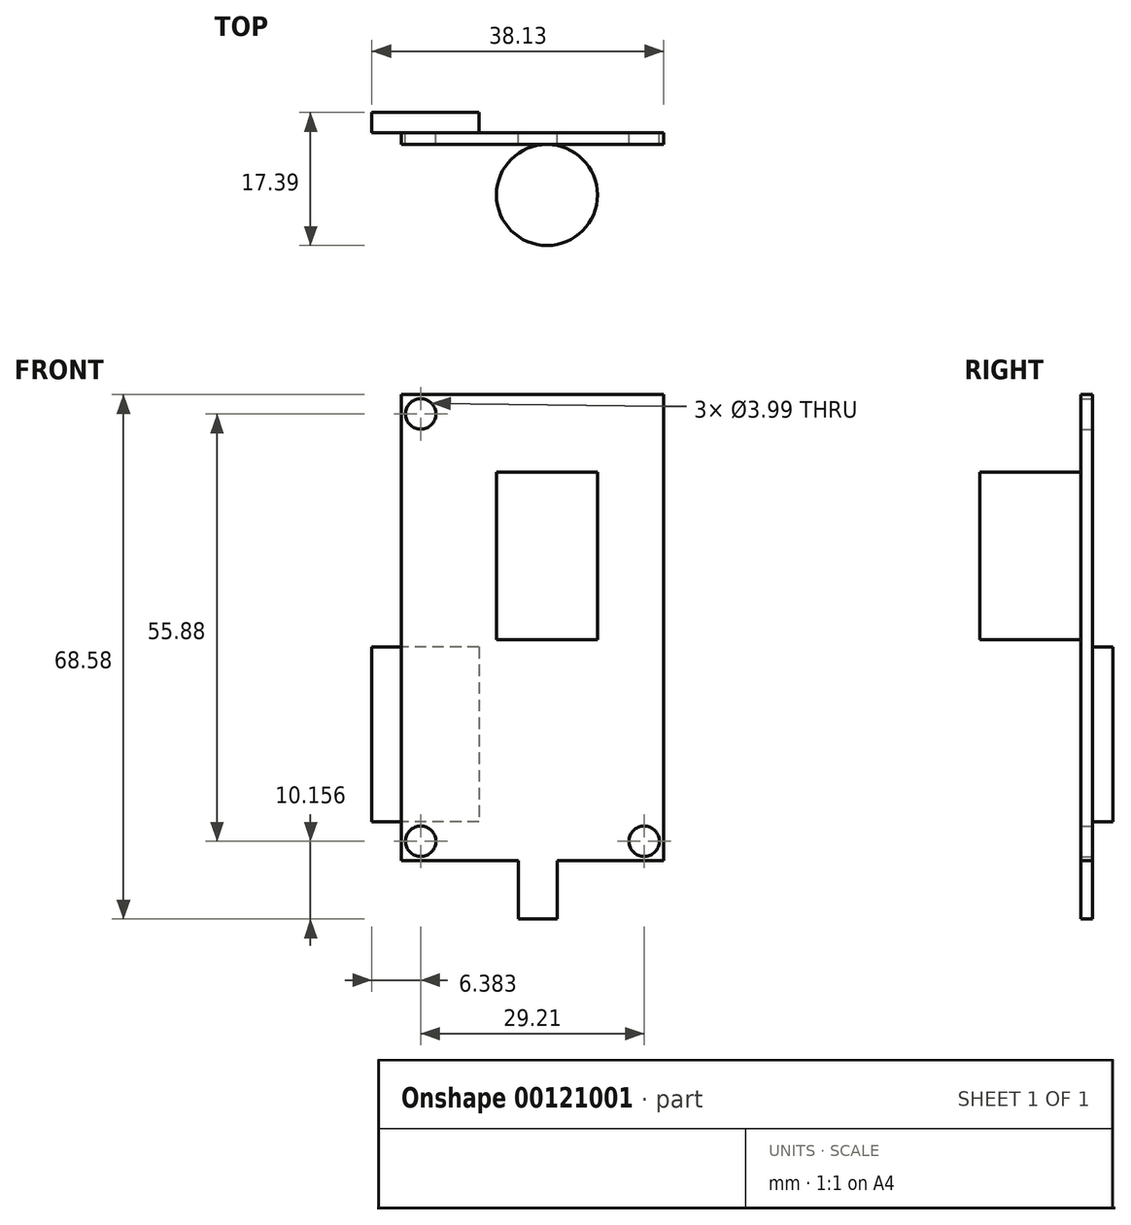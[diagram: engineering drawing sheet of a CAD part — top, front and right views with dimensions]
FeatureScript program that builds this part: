
annotation { "Feature Type Name" : "Feature", "Feature Type Description" : "" }
export const myFeature = defineFeature(function(context is Context, id is Id, definition is map)
    precondition{}
    {
        {
            var Q0;
            Q0=qCreatedBy(makeId("Front.planeOp"),FACE);
            var sketch = newSketch(context, id + "F0", { "sketchPlane" : qUnion([Q0])});
            skLineSegment(sketch, "E0.bottom", {"start": v(-17.68, 35.44) * mm, "end": v(16.61, 35.44) * mm});
            skLineSegment(sketch, "E0.top", {"start": v(-17.68, -25.52) * mm, "end": v(16.61, -25.52) * mm});
            skLineSegment(sketch, "E0.left", {"start": v(-17.68, 35.44) * mm, "end": v(-17.68, -25.52) * mm});
            skLineSegment(sketch, "E0.right", {"start": v(16.61, 35.44) * mm, "end": v(16.61, -25.52) * mm});
            skLineSegment(sketch, "E1.bottom", {"start": v(-2.36, -25.52) * mm, "end": v(2.72, -25.52) * mm});
            skLineSegment(sketch, "E1.top", {"start": v(-2.36, -33.14) * mm, "end": v(2.72, -33.14) * mm});
            skLineSegment(sketch, "E1.left", {"start": v(-2.36, -25.52) * mm, "end": v(-2.36, -33.14) * mm});
            skLineSegment(sketch, "E1.right", {"start": v(2.72, -25.52) * mm, "end": v(2.72, -33.14) * mm});
            skSolve(sketch);
        }
        {
            var Q0;
            Q0=qSketchRegion(id+"F0",true);
            extrude(context, id + "F1", {"entities" : qUnion([Q0]), "depth" : 1.52 * mm});
        }
        {
            var Q0;
            Q0=makeQuery(id+"F1.opExtrude","CAP_FACE",FACE,{"disambiguationData":[OSD([sQuery(id+"F0.wireOp",EDGE,"E0.bottom"),sQuery(id+"F0.wireOp",EDGE,"E0.top"),sQuery(id+"F0.wireOp",EDGE,"E0.left"),sQuery(id+"F0.wireOp",EDGE,"E0.right"),sQuery(id+"F0.wireOp",EDGE,"E1.top"),sQuery(id+"F0.wireOp",EDGE,"E1.left"),sQuery(id+"F0.wireOp",EDGE,"E1.right")])],"isStart":true});
            var sketch = newSketch(context, id + "F2", { "sketchPlane" : qUnion([Q0])});
            skLineSegment(sketch, "E2.bottom", {"start": v(7.52, 2.42) * mm, "end": v(21.52, 2.42) * mm});
            skLineSegment(sketch, "E2.top", {"start": v(7.52, -20.44) * mm, "end": v(21.52, -20.44) * mm});
            skLineSegment(sketch, "E2.left", {"start": v(7.52, 2.42) * mm, "end": v(7.52, -20.44) * mm});
            skLineSegment(sketch, "E2.right", {"start": v(21.52, 2.42) * mm, "end": v(21.52, -20.44) * mm});
            skSolve(sketch);
        }
        {
            var Q0;
            Q0=qSketchRegion(id+"F2",true);
            extrude(context, id + "F3", {"entities" : qUnion([Q0]), "operationType" : NewBodyOperationType.ADD, "depth" : 2.66 * mm});
        }
        {
            var Q0;
            Q0=makeQuery(id+"F1.opExtrude","SWEPT_FACE",FACE,{"disambiguationData":[OSD([sQuery(id+"F0.wireOp",EDGE,"E0.bottom")])]});
            cPlane(context, id + "F4", {"entities" : qUnion([Q0]), "cplaneType" : CPlaneType.OFFSET, "offset" : 10.16 * mm, "oppositeDirection" : true, "width" : 152.4 * mm, "height" : 152.4 * mm});
        }
        {
            var Q0;
            Q0=qCreatedBy(id+"F4.planeOp",FACE);
            var sketch = newSketch(context, id + "F5", { "sketchPlane" : qUnion([Q0])});
            skLineSegment(sketch, "E3", {"start": v(1.37, -1.52) * mm, "end": v(1.37, -14.73) * mm});
            skCircle(sketch, "E4", {"center": v(1.37, -8.13) * mm, "radius": 6.6 * mm});
            skPoint(sketch, "E5", {"position": v(-0.53, -1.52) * mm});
            skSolve(sketch);
        }
        {
            var Q0;
            Q0=qSketchRegion(id+"F5",true);
            extrude(context, id + "F6", {"entities" : qUnion([Q0]), "oppositeDirection" : true, "depth" : 21.9 * mm});
        }
        {
            var Q0;
            Q0=makeQuery(id+"F1.opExtrude","CAP_FACE",FACE,{"disambiguationData":[OSD([sQuery(id+"F0.wireOp",EDGE,"E0.bottom"),sQuery(id+"F0.wireOp",EDGE,"E0.top"),sQuery(id+"F0.wireOp",EDGE,"E0.left"),sQuery(id+"F0.wireOp",EDGE,"E0.right"),sQuery(id+"F0.wireOp",EDGE,"E1.top"),sQuery(id+"F0.wireOp",EDGE,"E1.left"),sQuery(id+"F0.wireOp",EDGE,"E1.right")])],"isStart":true});
            var sketch = newSketch(context, id + "F7", { "sketchPlane" : qUnion([Q0])});
            skCircle(sketch, "E6", {"center": v(15.14, 32.9) * mm, "radius": 2 * mm});
            skCircle(sketch, "E7", {"center": v(15.14, -22.98) * mm, "radius": 2 * mm});
            skCircle(sketch, "E8", {"center": v(-14.07, -22.98) * mm, "radius": 2 * mm});
            skLineSegment(sketch, "E9.bottom", {"start": v(-14.07, -22.98) * mm, "end": v(15.14, -22.98) * mm, "construction": true});
            skLineSegment(sketch, "E9.top", {"start": v(-14.07, 32.9) * mm, "end": v(15.14, 32.9) * mm, "construction": true});
            skLineSegment(sketch, "E9.left", {"start": v(-14.07, -22.98) * mm, "end": v(-14.07, 32.9) * mm, "construction": true});
            skLineSegment(sketch, "E9.right", {"start": v(15.14, -22.98) * mm, "end": v(15.14, 32.9) * mm, "construction": true});
            skSolve(sketch);
        }
        {
            var Q0;
            Q0=qSketchRegion(id+"F7",true);
            var Q1;
            Q1=sQuery(id+"F7.wireOp",EDGE,"E9.bottom");
            var Q2;
            Q2=sQuery(id+"F7.wireOp",EDGE,"E9.left");
            var Q3;
            Q3=sQuery(id+"F7.wireOp",EDGE,"E9.top");
            var Q4;
            Q4=sQuery(id+"F7.wireOp",EDGE,"E9.right");
            extrude(context, id + "F8", {"entities" : qUnion([Q0]), "operationType" : NewBodyOperationType.REMOVE, "surfaceEntities" : qUnion([Q1, Q2, Q3, Q4]), "endBound" : BoundingType.THROUGH_ALL, "oppositeDirection" : true, "depth" : 25.4 * mm});
        }
    });
